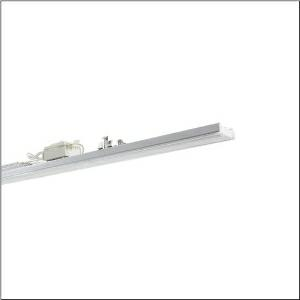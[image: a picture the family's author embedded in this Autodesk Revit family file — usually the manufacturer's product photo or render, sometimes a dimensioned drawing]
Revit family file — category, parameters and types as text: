
# Revit family: licross_r__21_recessed_mo_52tl107n485g_fff6
name_source: partatom
category: Lighting Fixtures
units: mm (PartAtom-declared; Revit-internal decimal feet)

## family parameters
Cut with Voids When Loaded = No
Host = Face
Light Source = No
Part Type = Normal
Room Calculation Point = No
Round Connector Dimension = Use Diameter
Shared = No

## types (1)
- Licross® 21 Recessed MO (1 x LED, 8580 lm, 47.9 W, 4000K)
    Apparent Load = 48 VA
    CIE Flux Codes = 50 81 96 100 100
    Color Rendering = 80
    Color Temperature = 4000K
    Default Elevation = 1800 mm
    Description = Licross® 21 Recessed MO, luminaire insert, of sheet steel, galvanised, coil coated, white, length: 1.500mm, width: 66mm, height: 67mm, LED rated luminous flux: 8.560lm, light colour: 840, control gear: ON/OFF, with plug, 3-pole, with phase selection, mains connection: 220..240V, AC, 50/60Hz, rated input power: 48W, halogen-free wiring, primary optical cover: cover, of PMMA, light emission: direct distribution, primary light characteristic: symmetric, protection rating (complete): IP40, insulation class (complete): insulation class I (protective earthing), certification: CE, ENEC, VDE, UKCA, protection symbol: D if used in an environment without relevant dust loads with corresponding accessories, impact resistance: IK06, permissible ambient temperature for indoor applications: -35..+40°C, corresponds to IFS (International Featured Standards) requirements for safety and quality in the food industry, reducing of maximum allowable ambient temperature of 5°C with ceiling mounting, LABS conformity tested according to VDMA 24364:2018-05, packaging unit: 1 piece
    Height = 58 mm
    Lamp = 1 x LED
    Lamp Light Flux = 8580 lm
    Lamp Power = 47.9 W
    Lamp count = 1
    Length = 1500 mm
    Luminous efficacy = 179 lm/W
    Manufacturer = Siteco
    ModVariant = No
    Model = 52TL107N485G
    Mounting Place = Ceiling
    Mounting Type = Pendant
    Number of Poles = 1
    OnlyDefault = Yes
    Power Factor = 1
    Product Name = Licross® 21 Recessed MO
    Product group = luminaire insert
    ProductGroupID = 902
    Protection Class = Protection class I
    Protection Degree = IP 40
    RLX_Detail_Level = 1
    RLX_Emergency_Light_Flux = 0 lm
    RLX_Emergency_Type = 0
    RLX_Emergency_Type_DB = No
    RlxData = <blob elided: 20717 chars, md5=0e744921>
    Socket = socket
    Standby Power = 0 W
    System Light Flux = 8580 lm
    System Power = 48 W
    Type Comments = Product without accessories
    Type Image = l_1296930.jpg
    URL = http://relux.com
    VarID = ---
    Voltage = 0 V
    Weight = 0.00 kg
    Width = 66 mm

## geometry (parser evidence)
native form markers: Blend x4, Sweep x11
no freeform markers — native parametric forms only
